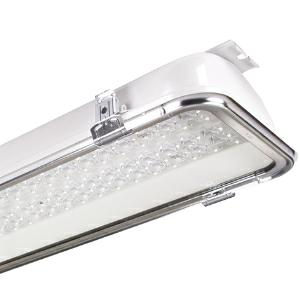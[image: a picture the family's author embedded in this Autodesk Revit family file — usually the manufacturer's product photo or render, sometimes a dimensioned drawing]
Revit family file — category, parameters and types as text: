
# Revit family: 3f_filippi_-_beta_235_76_vt_concentrato_3f_filippi_-_52513_-_beta_235_led_761x60_conc_vt_l1565
name_source: partatom
category: Lighting Fixtures
units: mm (PartAtom-declared; Revit-internal decimal feet)

## family parameters
Cut with Voids When Loaded = No
Host = Face
Light Source = No
Part Type = Normal
Room Calculation Point = No
Round Connector Dimension = Use Diameter
Shared = No

## types (1)
- 3F Filippi - Beta 235 76 VT Concentrato (1 x LED, 9792 lm, 65 W, 4000 K)
    Apparent Load = 65 VA
    Approval mark = CE
    CIE Flux Codes = 75 92 99 100 100
    Color Rendering = 80
    Color Temperature = 4000 K
    Control Gear = Electronic ballast
    Default Elevation = 1800 mm
    Description = ILLUMINOTECHNICAL
Luminous efficiency 100% (DLOR 100%, ULOR 0%).
Initial luminous flux of the luminaire 9792 lm.
Concentrated elliptical distribution.
Installation Interdistance Transv.D = 0.57 x hu - Long.D = 1.11 x hu.
Tabular UGR (CIE 117 - 4H-8H; S=0.25H; 70/50/20): RUG 18 - 19.5.
Beam angle: 36° - 73°.
Luminous efficacy 151 lm/W.
Lifetime (L93/B10): 30000 h. (tq+25°C)
Lifetime (L90/B10): 50000 h. (tq+25°C)
Lifetime (L85/B10): 80000 h. (tq+25°C)
Lifetime (L80/B10): 100000 h. (tq+25°C)
Lifetime (L85/B10): 50000 h. (tq+45°C)
Sudden decreased luminous flux after 50000 hours: 0% (C0).
Photobiological safety in compliance with IEC/TR 62778: RG0 risk exempt, (IEC 62471).
In compliance with IEC/EN 62722-2-1 - IEC/EN 62717 standards.

SOURCE
Linear LED module 60W/840.
Energy efficiency class (UE 2019/2020 - UE 2019/2015): C.
CIE 13.3 Colour rendering index: CRI >80 (R9 <50%).
IES TM-30 Fidelity Index: Rf = 84 Rg = 95.
CCT nominal colour temperature 4000 K.
Colour initial tolerance (MacAdam): SDCM 3.

MECHANICAL
Single-piece housing in pressed steel, powder-coated in white epoxy-polyester.
VT transparent glass, non-combustible, single-piece perimeter frame in galvanised steel.
Ecologic anti-aging injected sealing gasket.
Oversized gear-tray reflector unit in highly reflective white painted hot-galvanised steel.
Methacrylate (PMMA) lenses with external flat surface.
Galvanised steel snap-lock clips for diffuser mounting (safety n° 4 per fixture).
Luminaire with limited surface temperature. - D - (EN 60598-2-24)
Dimensions: 1565x235 mm, height 105 mm. Weight 11.45 kg.
IP66 protection degree.
Mechanical strength to impacts IK09 (10 joule).
Glow-wire test resistance 850°C.

ELECTRICAL
Halogen Free electronic wiring 230V-50/60Hz, power factor 0.95, THD <25%, constant output current, class I, 1 driver.
Power of the luminaire 65 W.
ENEC - CE.
Flicker: <4%.
Luminaire compliant with EN 60598-2-22 for power supply from a centralised emergency system CPSS (Central Power Supply System), not incorporated in the luminaire - high risk areas excluded. The default power and flux are 100% in AC and 100% in DC.
Ambient temperature from -20°C to +45°C.
Temperature class T6 max 85°C.
Quick connection via M20 3P connector with 9-13 mm tightening range.
Relative humidity UR: <85%.

INSTALLATION
Ceiling / Suspended / Wall.
All accessories dedicated to this product are available on the Catalog and on our website www.3F-Filippi.com.

APPLICATIONS
Dry, dusty indoor environments, subject to occasional water splashes.
Industrial environments, warehouses, environments where security locks are required on all clips, e.g. prisons (on request).
Environments in which it is necessary a total protection against falling fragments (eg environments with foodstuffs or machines with moving parts or with extreme temperature changes), use luminaires with laminated glass.
Tempered glass is not immune to falling fragments from harmless and caused by shocks or exceptionally derived from the tempering process.

WARNING
Fixture not suitable for cold stores with an ambient temperature <0°C and/or relative humidity >85%.
Luminaire designed for disposal/recycling at end-of-life.
Replaceable (LED only) light source by a professional. Replaceable control gear by a professional.
    Height = 105 mm
    Lamp = 1 x LED
    Lamp Light Flux = 9792 lm
    Lamp Power = 65 W
    Lamp count = 1
    Length = 1565 mm
    Lifetime = 50000 h
    Luminous efficacy = 151 lm/W
    Manufacturer = 3F Filippi
    ModVariant = No
    Model = 3F Filippi - 52513 - Beta 235 LED 761x60 CONC VT L1565
    Mounting Place = Ceiling
    Mounting Type = Pendant
    Number of Poles = 1
    OnlyDefault = Yes
    Power Factor = 1
    Product Name = 3F Filippi - Beta 235 76 VT Concentrato
    Product group = pendant luminaire
    ProductGroupID = 9
    Protection Class = Protection class I
    Protection Degree = IP 66
    RLX_Detail_Level = 1
    RLX_Emergency_Light_Flux = 0 lm
    RLX_Emergency_Type = 0
    RLX_Emergency_Type_DB = No
    RlxData = <blob elided: 90153 chars, md5=e8ffe95f>
    Socket = socket
    Standby Power = 0 W
    System Light Flux = 9792 lm
    System Power = 65 W
    Type Comments = Product without accessories
    Type Image = 3ffilippi_beta_235_led_76_vt.jpg
    URL = http://relux.com
    VarID = ---
    Voltage = 0 V
    Weight = 0.00 kg
    Width = 235 mm

## geometry (parser evidence)
native form markers: Blend x4, Sweep x11
no freeform markers — native parametric forms only
